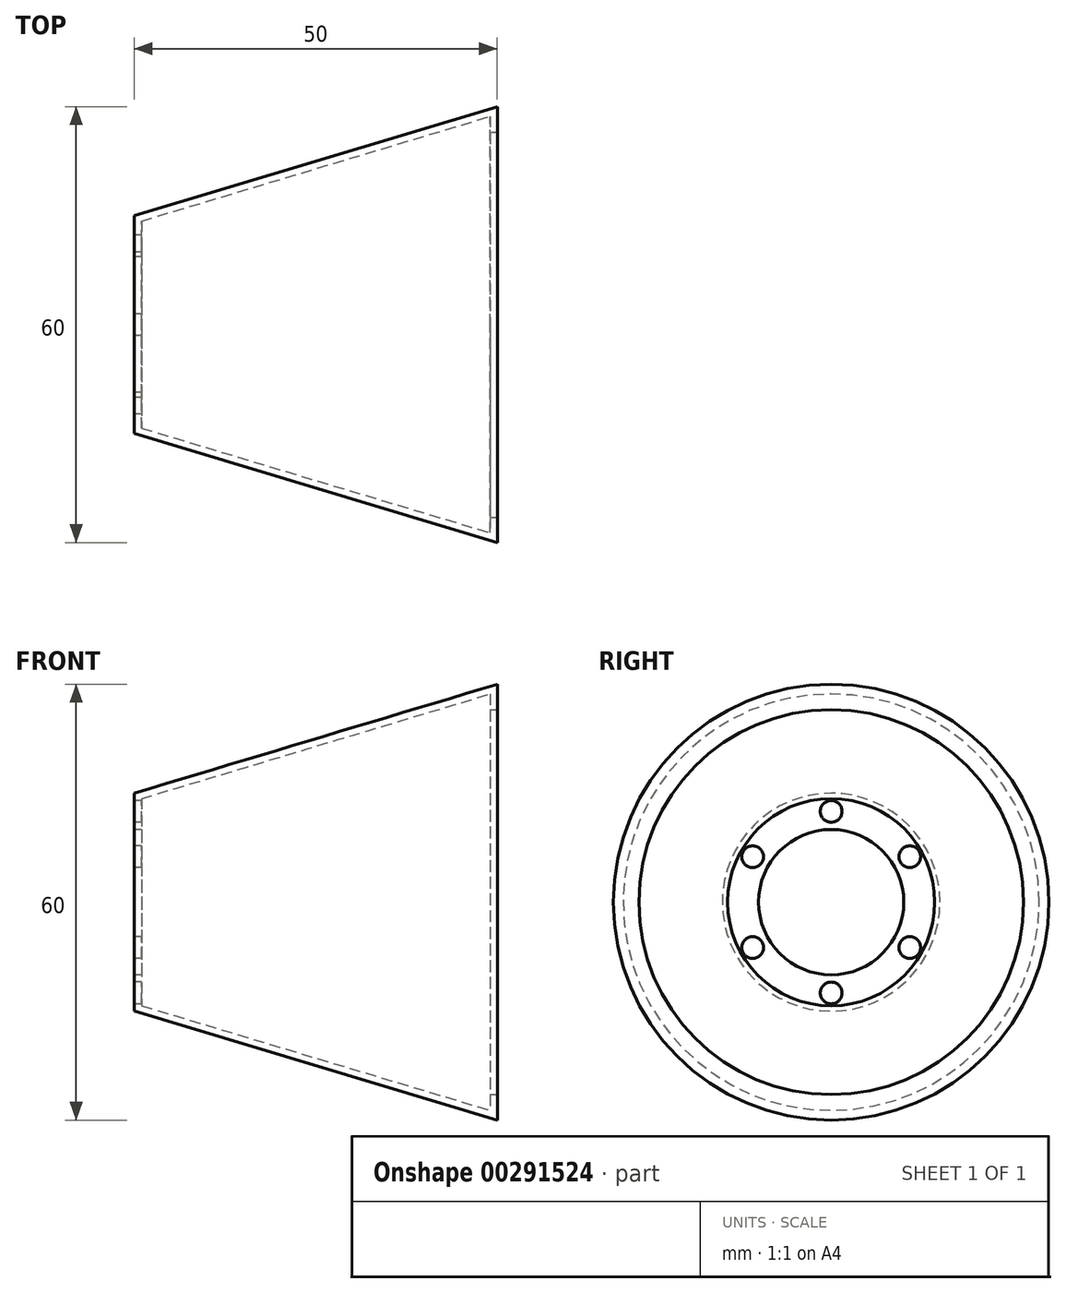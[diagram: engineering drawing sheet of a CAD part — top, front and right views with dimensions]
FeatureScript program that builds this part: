
annotation { "Feature Type Name" : "Feature", "Feature Type Description" : "" }
export const myFeature = defineFeature(function(context is Context, id is Id, definition is map)
    precondition{}
    {
        {
            var Q0;
            Q0=qCreatedBy(makeId("Front.planeOp"),FACE);
            var sketch = newSketch(context, id + "F0", { "sketchPlane" : qUnion([Q0])});
            skLineSegment(sketch, "E0", {"start": v(-17.63, 10) * mm, "end": v(32.37, 10) * mm});
            skLineSegment(sketch, "E1", {"start": v(-17.63, 15) * mm, "end": v(32.37, 30) * mm});
            skLineSegment(sketch, "E2", {"start": v(-17.63, 15) * mm, "end": v(-17.63, 10) * mm});
            skLineSegment(sketch, "E3", {"start": v(32.37, 10) * mm, "end": v(32.37, 30) * mm});
            skLineSegment(sketch, "E4", {"start": v(31.37, 11) * mm, "end": v(31.37, 28.66) * mm});
            skLineSegment(sketch, "E5", {"start": v(31.37, 28.66) * mm, "end": v(-16.63, 14.26) * mm});
            skLineSegment(sketch, "E6", {"start": v(-16.63, 14.26) * mm, "end": v(-16.63, 11) * mm});
            skLineSegment(sketch, "E7", {"start": v(-16.63, 11) * mm, "end": v(31.37, 11) * mm});
            skSolve(sketch);
        }
        {
            var Q0;
            Q0=qCreatedBy(makeId("Front.planeOp"),FACE);
            var sketch = newSketch(context, id + "F1", { "sketchPlane" : qUnion([Q0])});
            skLineSegment(sketch, "E8", {"start": v(-40.54, 0) * mm, "end": v(65.4, 0) * mm});
            skSolve(sketch);
        }
        {
            var Q0;
            Q0 = qSketchRegion(id + "F0", true);
            var Q1;
            Q1=sQuery(id+"F1.wireOp",EDGE,"E8");
            revolve(context, id + "F2", {"entities" : qUnion([Q0]), "axis" : qUnion([Q1]), "revolveType" : RevolveType.FULL});
        }
        {
            var Q0;
            Q0=makeQuery(id+"F2.opRevolve","SWEPT_FACE",FACE,{"disambiguationData":[OSD([sQuery(id+"F0.wireOp",EDGE,"E3")])]});
            var sketch = newSketch(context, id + "F3", { "sketchPlane" : qUnion([Q0])});
            skCircle(sketch, "E9", {"center": v(0, 0) * mm, "radius": 11 * mm});
            skCircle(sketch, "E10", {"center": v(0, 0) * mm, "radius": 26.5 * mm});
            skSolve(sketch);
        }
        {
            var Q0;
            Q0=makeQuery(id+"F3.imprint","IMPRINT",FACE,{"disambiguationData":[TD([[makeQuery(id+"F3.imprint","IMPRINT",EDGE,{"derivedFrom":sQuery(id+"F3.wireOp",EDGE,"E9")}),-1.0]])]});
            extrude(context, id + "F4", {"entities" : qUnion([Q0]), "operationType" : NewBodyOperationType.REMOVE, "oppositeDirection" : true, "depth" : 1.1 * mm});
        }
        {
            var Q0;
            Q0=makeQuery(id+"F2.opRevolve","SWEPT_FACE",FACE,{"disambiguationData":[OSD([sQuery(id+"F0.wireOp",EDGE,"E2")])]});
            var sketch = newSketch(context, id + "F5", { "sketchPlane" : qUnion([Q0])});
            skCircle(sketch, "E11", {"center": v(0, 12.5) * mm, "radius": 1.5 * mm});
            skCircle(sketch, "E12.1.0", {"center": v(-10.83, 6.25) * mm, "radius": 1.5 * mm});
            skCircle(sketch, "E12.2.0", {"center": v(-10.83, -6.25) * mm, "radius": 1.5 * mm});
            skCircle(sketch, "E12.3.0", {"center": v(0, -12.5) * mm, "radius": 1.5 * mm});
            skCircle(sketch, "E12.4.0", {"center": v(10.83, -6.25) * mm, "radius": 1.5 * mm});
            skCircle(sketch, "E12.5.0", {"center": v(10.83, 6.25) * mm, "radius": 1.5 * mm});
            skPoint(sketch, "E12.center", {"position": v(0, 0) * mm});
            skSolve(sketch);
        }
        {
            var Q0;
            Q0=makeQuery(id+"F5.imprint","IMPRINT",FACE,{"disambiguationData":[TD([[makeQuery(id+"F5.imprint","IMPRINT",EDGE,{"derivedFrom":sQuery(id+"F5.wireOp",EDGE,"E11")}),1.0]])]});
            var Q1;
            Q1=makeQuery(id+"F5.imprint","IMPRINT",FACE,{"disambiguationData":[TD([[makeQuery(id+"F5.imprint","IMPRINT",EDGE,{"derivedFrom":sQuery(id+"F5.wireOp",EDGE,"E12.1.0")}),1.0]])]});
            var Q2;
            Q2=makeQuery(id+"F5.imprint","IMPRINT",FACE,{"disambiguationData":[TD([[makeQuery(id+"F5.imprint","IMPRINT",EDGE,{"derivedFrom":sQuery(id+"F5.wireOp",EDGE,"E12.2.0")}),1.0]])]});
            var Q3;
            Q3=makeQuery(id+"F5.imprint","IMPRINT",FACE,{"disambiguationData":[TD([[makeQuery(id+"F5.imprint","IMPRINT",EDGE,{"derivedFrom":sQuery(id+"F5.wireOp",EDGE,"E12.3.0")}),1.0]])]});
            var Q4;
            Q4=makeQuery(id+"F5.imprint","IMPRINT",FACE,{"disambiguationData":[TD([[makeQuery(id+"F5.imprint","IMPRINT",EDGE,{"derivedFrom":sQuery(id+"F5.wireOp",EDGE,"E12.4.0")}),1.0]])]});
            var Q5;
            Q5=makeQuery(id+"F5.imprint","IMPRINT",FACE,{"disambiguationData":[TD([[makeQuery(id+"F5.imprint","IMPRINT",EDGE,{"derivedFrom":sQuery(id+"F5.wireOp",EDGE,"E12.5.0")}),1.0]])]});
            extrude(context, id + "F6", {"entities" : qUnion([Q0, Q1, Q2, Q3, Q4, Q5]), "operationType" : NewBodyOperationType.REMOVE, "oppositeDirection" : true, "depth" : 2 * mm});
        }
        {
            var Q0;
            Q0=makeQuery(id+"F4.boolean.opBoolean","SPLIT",FACE,{"disambiguationData":[TD([makeQuery(id+"F2.opRevolve","SWEPT_FACE",FACE,{"disambiguationData":[OSD([sQuery(id+"F0.wireOp",EDGE,"E0")])]})])],"derivedFrom":makeQuery(id+"F2.opRevolve","SWEPT_FACE",FACE,{"disambiguationData":[OSD([sQuery(id+"F0.wireOp",EDGE,"E3")])]})});
            extrude(context, id + "F7", {"entities" : qUnion([Q0]), "operationType" : NewBodyOperationType.REMOVE, "oppositeDirection" : true, "depth" : 49 * mm});
        }
    });
